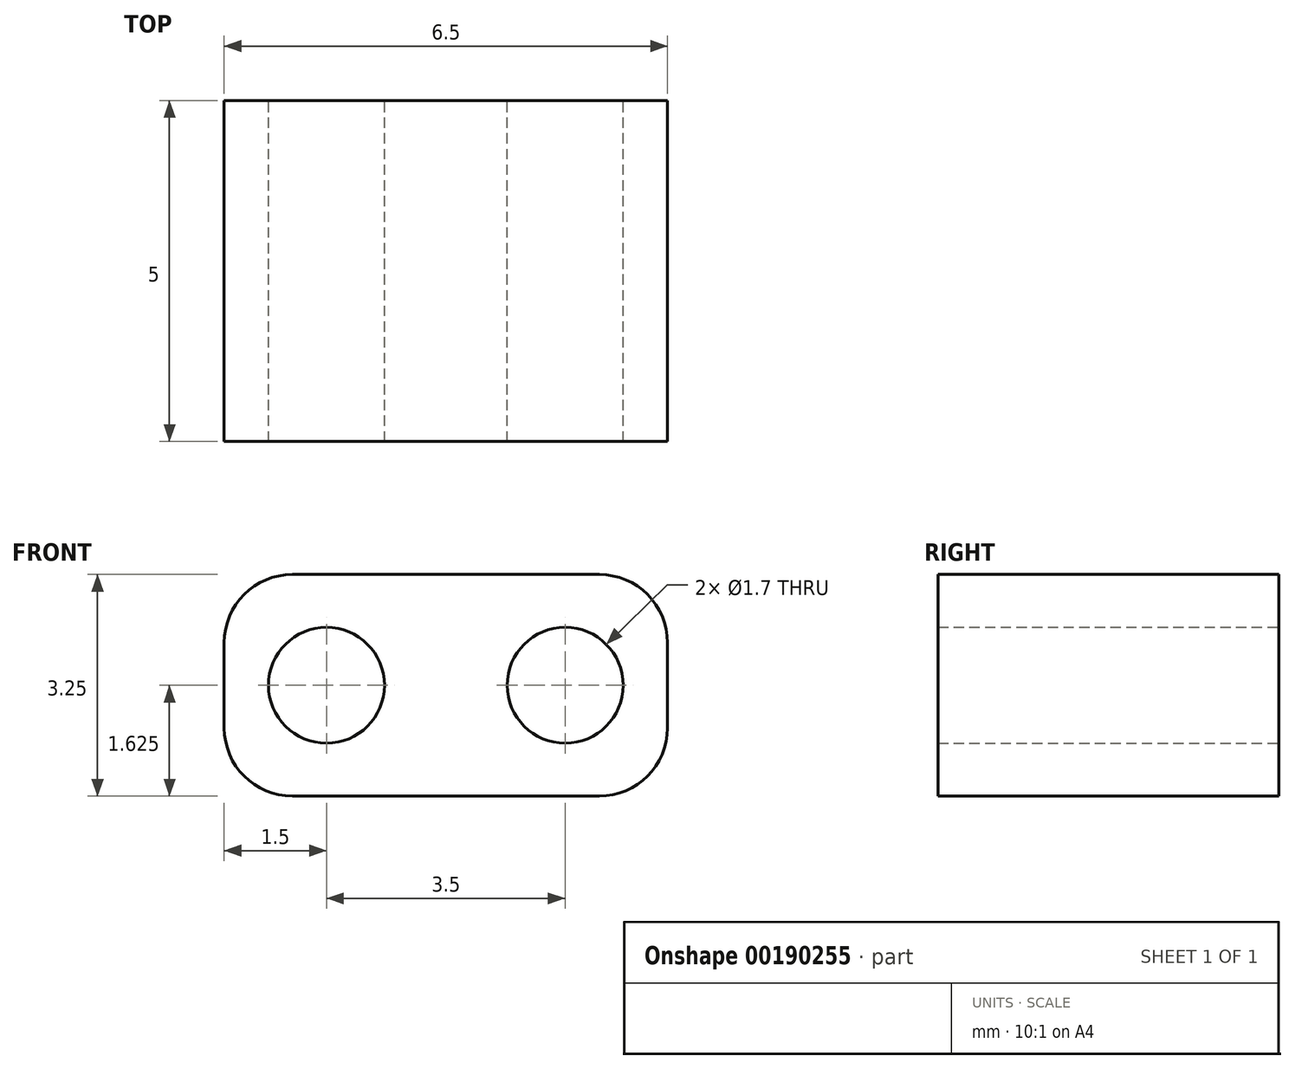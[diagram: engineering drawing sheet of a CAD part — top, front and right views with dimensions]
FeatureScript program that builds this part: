
annotation { "Feature Type Name" : "Feature", "Feature Type Description" : "" }
export const myFeature = defineFeature(function(context is Context, id is Id, definition is map)
    precondition{}
    {
        {
            var Q0;
            Q0=qCreatedBy(makeId("Front.planeOp"),FACE);
            var sketch = newSketch(context, id + "F0", { "sketchPlane" : qUnion([Q0])});
            skLineSegment(sketch, "E0", {"start": v(0, 0) * mm, "end": v(-2.25, 0) * mm});
            skLineSegment(sketch, "E1", {"start": v(-3.25, 1) * mm, "end": v(-3.25, 2.25) * mm});
            skLineSegment(sketch, "E2", {"start": v(-2.25, 3.25) * mm, "end": v(0, 3.25) * mm});
            skCircle(sketch, "E3", {"center": v(-1.75, 1.63) * mm, "radius": 0.85 * mm});
            skPoint(sketch, "E3.centerSnap0", {"position": v(-3.25, 1.63) * mm});
            skLineSegment(sketch, "E4", {"start": v(0, 3.25) * mm, "end": v(0, 0) * mm, "construction": true});
            skPoint(sketch, "E5.visualSharp", {"position": v(-3.25, 3.25) * mm});
            skArc(sketch, "E5.filletArc", {"start": v(-2.25, 3.25) * mm, "mid": v(-2.96, 2.96) * mm, "end": v(-3.25, 2.25) * mm});
            skPoint(sketch, "E6.visualSharp", {"position": v(-3.25, 0) * mm});
            skArc(sketch, "E6.filletArc", {"start": v(-3.25, 1) * mm, "mid": v(-2.96, 0.3) * mm, "end": v(-2.25, 0) * mm});
            skLineSegment(sketch, "E7.MirrorCS", {"start": v(2.25, 3.25) * mm, "end": v(0, 3.25) * mm});
            skLineSegment(sketch, "E8.MirrorCS", {"start": v(3.25, 1) * mm, "end": v(3.25, 2.25) * mm});
            skLineSegment(sketch, "E9.MirrorCS", {"start": v(0, 0) * mm, "end": v(2.25, 0) * mm});
            skArc(sketch, "E10.MirrorCS", {"start": v(3.25, 1) * mm, "mid": v(2.96, 0.3) * mm, "end": v(2.25, 0) * mm});
            skArc(sketch, "E11.MirrorCS", {"start": v(2.25, 3.25) * mm, "mid": v(2.96, 2.96) * mm, "end": v(3.25, 2.25) * mm});
            skCircle(sketch, "E12.MirrorC", {"center": v(1.75, 1.63) * mm, "radius": 0.85 * mm});
            skSolve(sketch);
        }
        {
            var Q0;
            Q0 = qSketchRegion(id + "F0", true);
            extrude(context, id + "F1", {"entities" : qUnion([Q0]), "depth" : 5 * mm});
        }
    });
